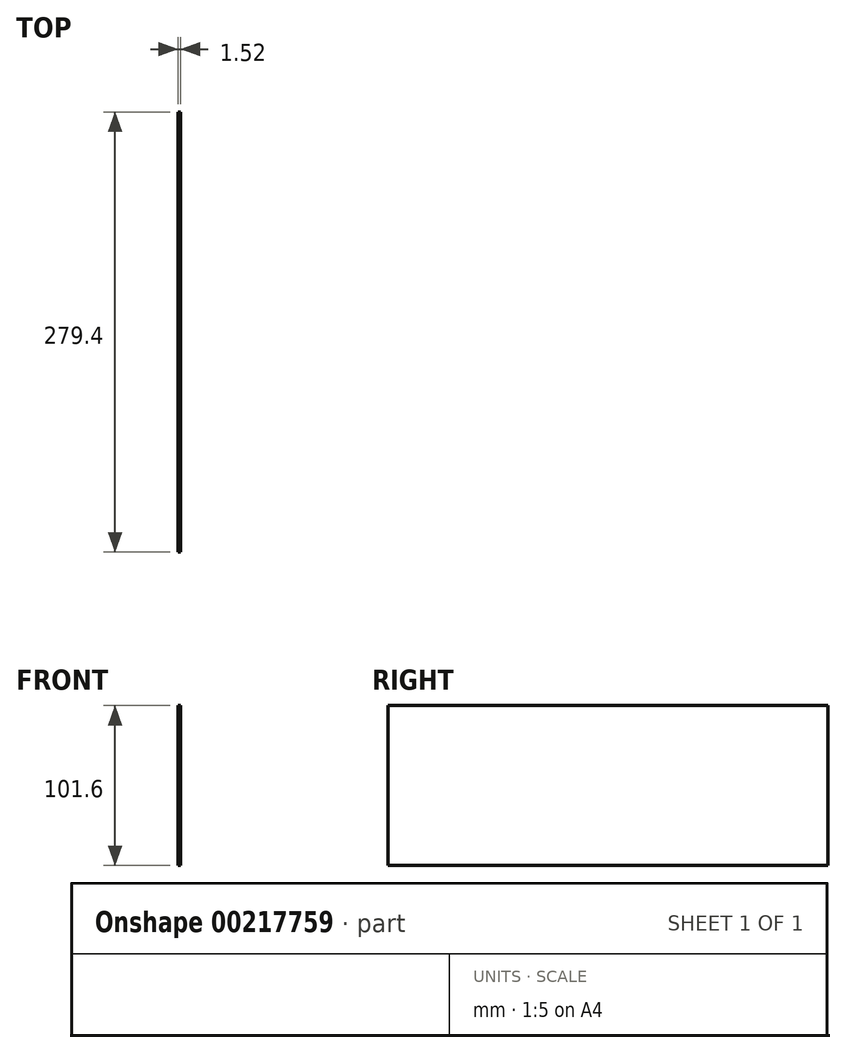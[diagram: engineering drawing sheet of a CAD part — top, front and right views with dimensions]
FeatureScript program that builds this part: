
annotation { "Feature Type Name" : "Feature", "Feature Type Description" : "" }
export const myFeature = defineFeature(function(context is Context, id is Id, definition is map)
    precondition{}
    {
        {
            var Q0;
            Q0=qCreatedBy(makeId("Right.planeOp"),FACE);
            var sketch = newSketch(context, id + "F0", { "sketchPlane" : qUnion([Q0])});
            skLineSegment(sketch, "E0.bottom", {"start": v(-112.65, 49.56) * mm, "end": v(166.75, 49.56) * mm});
            skLineSegment(sketch, "E0.top", {"start": v(-112.65, -52.04) * mm, "end": v(166.75, -52.04) * mm});
            skLineSegment(sketch, "E0.left", {"start": v(-112.65, 49.56) * mm, "end": v(-112.65, -52.04) * mm});
            skLineSegment(sketch, "E0.right", {"start": v(166.75, 49.56) * mm, "end": v(166.75, -52.04) * mm});
            skSolve(sketch);
        }
        {
            var Q0;
            Q0 = qSketchRegion(id + "F0", true);
            extrude(context, id + "F1", {"entities" : qUnion([Q0]), "depth" : 1.52 * mm});
        }
    });
